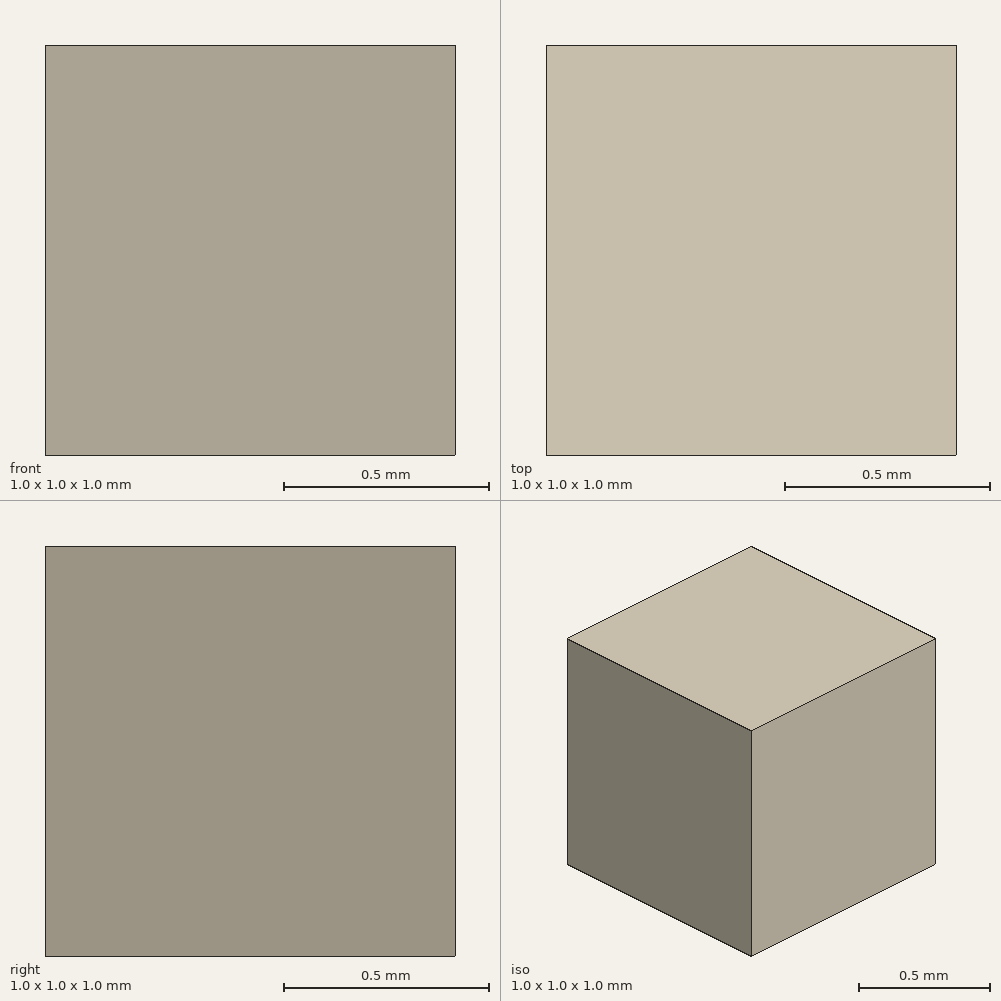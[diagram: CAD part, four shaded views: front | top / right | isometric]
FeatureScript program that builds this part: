
annotation { "Feature Type Name" : "Feature", "Feature Type Description" : "" }
export const myFeature = defineFeature(function(context is Context, id is Id, definition is map)
    precondition{}
    {
        {
            var Q0;
            Q0=qCreatedBy(makeId("Top.planeOp"),FACE);
            var sketch = newSketch(context, id + "F0", { "sketchPlane" : qUnion([Q0])});
            skLineSegment(sketch, "E0.bottom", {"start": v(-0.5, 0.5) * mm, "end": v(0.5, 0.5) * mm});
            skLineSegment(sketch, "E0.top", {"start": v(-0.5, -0.5) * mm, "end": v(0.5, -0.5) * mm});
            skLineSegment(sketch, "E0.left", {"start": v(-0.5, 0.5) * mm, "end": v(-0.5, -0.5) * mm});
            skLineSegment(sketch, "E0.right", {"start": v(0.5, 0.5) * mm, "end": v(0.5, -0.5) * mm});
            skPoint(sketch, "E0.middle", {"position": v(0, 0) * mm});
            skLineSegment(sketch, "E1.bottom", {"start": v(-0.7, 0.7) * mm, "end": v(0.7, 0.7) * mm});
            skLineSegment(sketch, "E1.top", {"start": v(-0.7, -0.7) * mm, "end": v(0.7, -0.7) * mm});
            skLineSegment(sketch, "E1.left", {"start": v(-0.7, 0.7) * mm, "end": v(-0.7, -0.7) * mm});
            skLineSegment(sketch, "E1.right", {"start": v(0.7, 0.7) * mm, "end": v(0.7, -0.7) * mm});
            skSolve(sketch);
        }
        {
            var Q0;
            Q0=makeQuery(id+"F0.imprint","IMPRINT",FACE,{"disambiguationData":[TD([[makeQuery(id+"F0.imprint","IMPRINT",EDGE,{"derivedFrom":sQuery(id+"F0.wireOp",EDGE,"E0.bottom")}),-1.0]])]});
            extrude(context, id + "F1", {"entities" : qUnion([Q0]), "depth" : 1 * mm});
        }
    });
